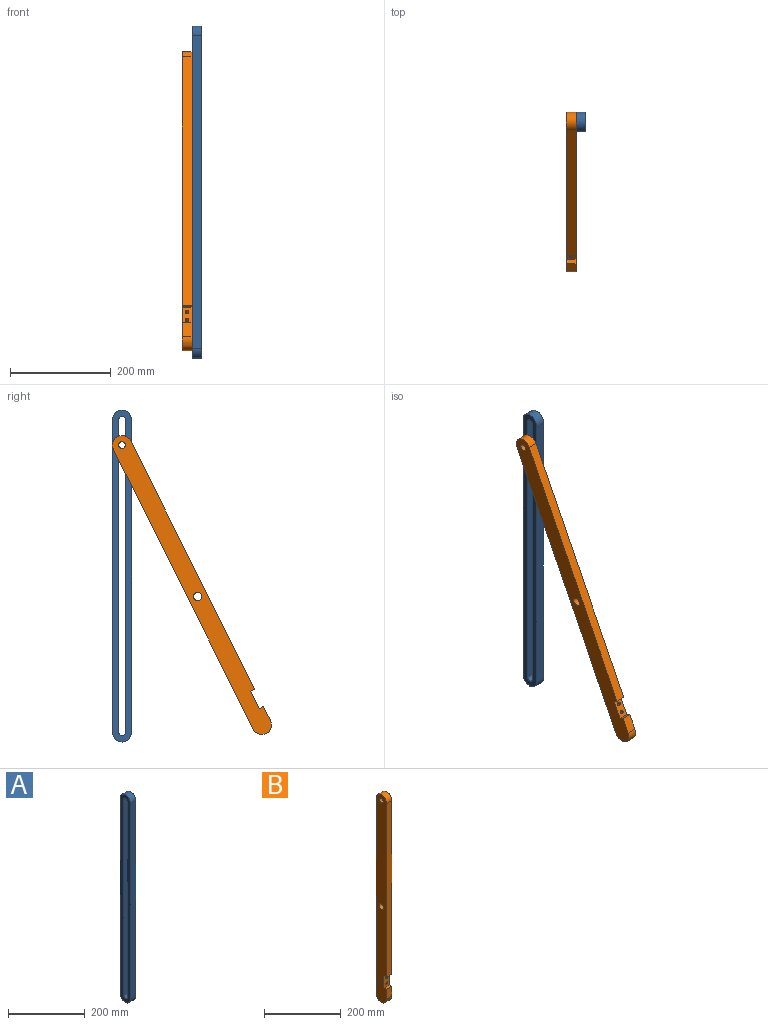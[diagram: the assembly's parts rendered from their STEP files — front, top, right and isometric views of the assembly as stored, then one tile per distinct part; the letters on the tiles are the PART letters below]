
ASSEMBLY  parts=2 mates=1
PART A: 10 faces, bbox 19.1x38.1x660.4 mm
  f0: plane 660.4x38.1mm, normal (1,0,0), area 16310.4mm2, adj f1,f2,f3,f4,f5,f7,f8,f9
  f1: cylinder r=6.75mm len=19.05mm, axis (-1,0,0), area 403.7mm2, adj f0,f6,f7,f8
  f2: plane 622.3x19.05mm, normal (0,-1,0), area 11854.8mm2, adj f0,f3,f5,f6
  f3: cylinder r=19.05mm len=38.1mm, axis (-1,0,0), area 1140.1mm2, adj f0,f2,f4,f6
  f4: plane 622.3x19.05mm, normal (0,1,0), area 11854.8mm2, adj f0,f3,f5,f6
  f5: cylinder r=19.05mm len=38.1mm, axis (-1,0,0), area 1140.1mm2, adj f0,f2,f4,f6
  f6: plane 660.4x38.1mm, normal (-1,0,0), area 16310.4mm2, adj f1,f2,f3,f4,f5,f7,f8,f9
  f7: plane 622.3x19.05mm, normal (0,-1,0), area 11854.8mm2, adj f0,f1,f6,f9
  f8: plane 622.3x19.05mm, normal (0,1,0), area 11854.8mm2, adj f0,f1,f6,f9
  f9: cylinder r=6.75mm len=19.05mm, axis (1,0,0), area 403.7mm2, adj f0,f6,f7,f8
PART B: 16 faces, bbox 19.1x38.1x660.4 mm
  f0: plane 552.45x19.05mm, normal (0,-1,0), area 10524.2mm2, adj f1,f5,f6,f9
  f1: plane 660.4x38.1mm, normal (1,0,0), area 24125.7mm2, adj f0,f2,f3,f4,f5,f7,f8,f9
  f2: plane 31.75x19.05mm, normal (0,-1,0), area 604.8mm2, adj f1,f3,f6,f10
  f3: cylinder r=19.05mm len=38.1mm, axis (-1,0,0), area 1140.1mm2, adj f1,f2,f4,f6
  f4: plane 622.3x19.05mm, normal (0,1,0), area 11854.8mm2, adj f1,f3,f5,f6
  f5: cylinder r=19.05mm len=38.1mm, axis (-1,0,0), area 1140.1mm2, adj f0,f1,f4,f6
  f6: plane 660.4x38.1mm, normal (-1,0,0), area 24125.7mm2, adj f0,f2,f3,f4,f5,f7,f8,f9
  f7: cylinder r=8.33mm len=19.05mm, axis (-1,0,0), area 997.5mm2, adj f1,f6
  f8: cylinder r=6.75mm len=19.05mm, axis (-1,0,0), area 807.5mm2, adj f1,f6
  f9: plane 19.05x9.53mm, normal (0,0,-1), area 181.5mm2, adj f0,f1,f6,f11
  f10: plane 19.05x9.53mm, normal (0,0,1), area 181.5mm2, adj f1,f2,f6,f11
  f11: plane 38.1x19.05mm, normal (0,-1,0), area 654.1mm2, adj f1,f6,f9,f10,f13,f15
  f12: cone r=0mm half-angle=59deg, axis (0,-1,0), area 41.8mm2, adj f13
  f13: cylinder r=3.38mm len=15.88mm, axis (0,-1,0), area 337mm2, adj f11,f12
  f14: cone r=0mm half-angle=59deg, axis (0,-1,0), area 41.8mm2, adj f15
  f15: cylinder r=3.38mm len=15.88mm, axis (0,-1,0), area 337mm2, adj f11,f14
PLACE A at identity fixed
PLACE B rot(axis=(-1,0,0),26.6deg) t=(-19.05,-284.88,25.35)mm
MATE pin_slot B.f5 <-> A.f1  axis (1,0,0) through (0,19.05,590.43)mm
